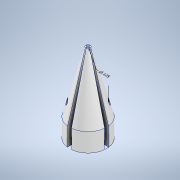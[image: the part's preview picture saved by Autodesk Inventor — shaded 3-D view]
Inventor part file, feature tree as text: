
AUTODESK INVENTOR PART (.ipt)
format: ipt  version: 2022 (Build 260153000, 153)  size: 357,888 bytes
history: native  units: in
note: dims shown in document units (in); Inventor stores cm internally (conversion verified against a paired STEP export)
features: sketch x6, loft x5, extrude x4, other x3, revolve x1, plane x1, hole x1
ambient origin geometry x8: Origin, YZ Plane, XZ Plane, XY Plane, X Axis, Y Axis, Z Axis, Center Point
bodies: Solid1 (feature_tree), Solid2 (feature_tree), Solid3 (feature_tree)
feature tree (21):
  other  "Annotations"
  extrude  "Extrusion1"  Depth=0.5in TaperAngle=0.0deg
  revolve  "Revolution1"  Angle=75.0deg
  sketch  "Sketch4"  dims[d5=90.0deg d6=1.6328in]
  sketch  "Sketch5"  dims[d7=0.4in d8=0.0625in]
  sketch  "Sketch6"  dims[d9=0.0625in d10=0.0625in]
  extrude  "Extrusion2"  Depth=1.6328in
  extrude  "Extrusion3"  Depth=0.0625in
  loft  "Loft1"
  loft  "Loft2"
  loft  "Loft3"
  loft  "Loft4"
  loft  "Loft5"
  plane  "Work Plane1"
  extrude  "Extrusion4"  Depth=0.0125in
  sketch  "Sketch1"  dims[d0=1.0in d1=0.5in d2=0.0in]
  sketch  "Sketch2"  dims[d3=0.0625in d4=75.0deg]
  sketch  "Sketch7"  dims[d11=0.0625in d16=0.0625in d17=0.0125in d18=0.0125in d19=0.0125in d20=0.0125in d22=0.5in d23=0.0in d24=0.5in d25=0.0in d26=0.0125in d27=0.0125in d28=0.0in d29=90.0deg d30=0.0in d31=90.0deg d32=0.0in d33=90.0deg d34=0.0in d35=90.0deg d36=0.0in d37=90.0deg d38=0.0in d39=90.0deg d40=0.0in d41=90.0deg d42=0.0in d43=90.0deg d44=0.0in d45=90.0deg d46=0.5in d47=0.5in d48=0.5in d49=0.5in d50=0.08in d51=0.08in d52=0.08in d53=0.08in d54=0.0in d55=90.0deg d56=0.0in d57=90.0deg d58=0.0in d59=90.0deg d60=0.0in d61=90.0deg d62=0.0in d63=90.0deg d64=0.0in d65=90.0deg d66=45.0deg d67=0.1417in d68=0.85in d69=0.0in d70=0.0in d12=1.5661in d13=1.0in d14=0.9835in d15=0.125in d71=0.3384in d72=0.3407in d73=0.0181in]
  other  "Diameter Dimension 1"
  other  "Diameter Dimension 2"
  hole  "Hole Note 1"  [1 undecoded]
note: 1 required parameter value undecoded (feature->parameter linkage not recoverable at this tier; creation-order binding heuristic only, values carry confidence <= 0.55)
